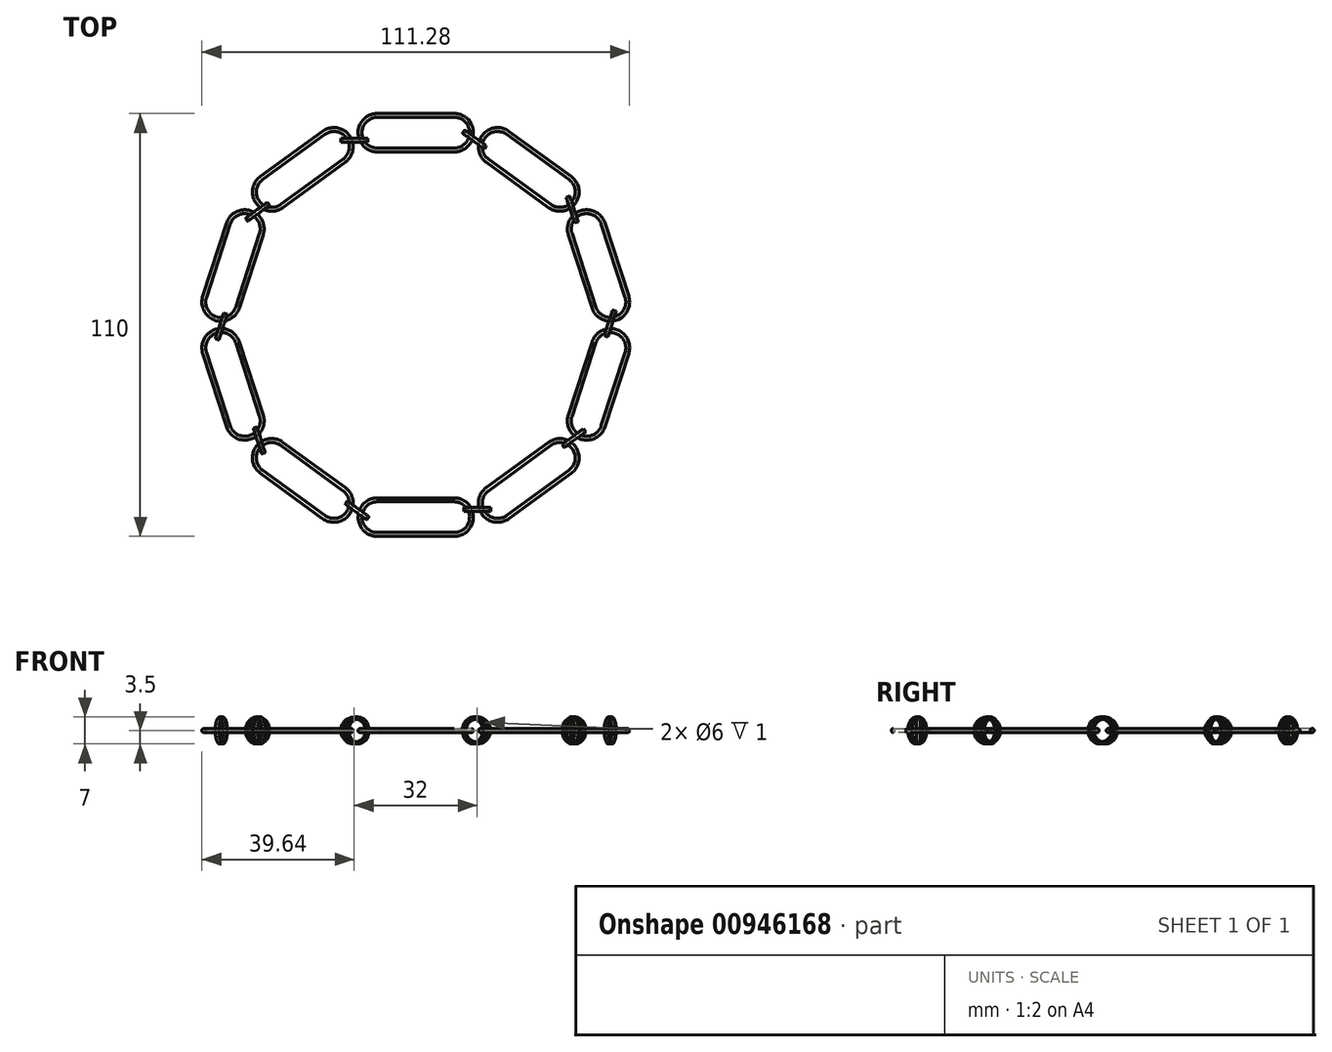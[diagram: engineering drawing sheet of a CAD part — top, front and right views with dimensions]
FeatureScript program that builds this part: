
annotation { "Feature Type Name" : "Feature", "Feature Type Description" : "" }
export const myFeature = defineFeature(function(context is Context, id is Id, definition is map)
    precondition{}
    {
        {
            var Q0;
            Q0=qCreatedBy(makeId("Top.planeOp"),FACE);
            var sketch = newSketch(context, id + "F0", { "sketchPlane" : qUnion([Q0])});
            skArc(sketch, "E0", {"start": v(-10, -45) * mm, "mid": v(-15, -50) * mm, "end": v(-10, -55) * mm});
            skArc(sketch, "E1", {"start": v(10, -55) * mm, "mid": v(15, -50) * mm, "end": v(10, -45) * mm});
            skLineSegment(sketch, "E2", {"start": v(-10, -45) * mm, "end": v(10, -45) * mm});
            skLineSegment(sketch, "E3", {"start": v(-10, -55) * mm, "end": v(10, -55) * mm});
            skLineSegment(sketch, "E4", {"start": v(-10, -50) * mm, "end": v(10, -50) * mm, "construction": true});
            skPoint(sketch, "E5", {"position": v(0, -50) * mm});
            skLineSegment(sketch, "E6.0", {"start": v(-10, -46) * mm, "end": v(10, -46) * mm});
            skArc(sketch, "E6.1", {"start": v(-10, -46) * mm, "mid": v(-14, -50) * mm, "end": v(-10, -54) * mm});
            skLineSegment(sketch, "E6.2", {"start": v(-10, -54) * mm, "end": v(10, -54) * mm});
            skArc(sketch, "E6.3", {"start": v(10, -54) * mm, "mid": v(14, -50) * mm, "end": v(10, -46) * mm});
            skSolve(sketch);
        }
        {
            var Q0;
            Q0=makeQuery(id+"F0.imprint","IMPRINT",FACE,{"disambiguationData":[TD([[makeQuery(id+"F0.imprint","IMPRINT",EDGE,{"derivedFrom":sQuery(id+"F0.wireOp",EDGE,"E0")}),1.0]])]});
            extrude(context, id + "F1", {"entities" : qUnion([Q0]), "depth" : 1 * mm, "offsetDistance" : 25 * mm});
        }
        {
            var Q0;
            Q0=makeQuery(id+"F1.opExtrude","CAP_EDGE",EDGE,{"disambiguationData":[OSD([sQuery(id+"F0.wireOp",EDGE,"E6.0")])],"isStart":false});
            var Q1;
            Q1=makeQuery(id+"F1.opExtrude","CAP_EDGE",EDGE,{"disambiguationData":[OSD([sQuery(id+"F0.wireOp",EDGE,"E6.0")])],"isStart":true});
            var Q2;
            Q2=makeQuery(id+"F1.opExtrude","CAP_EDGE",EDGE,{"disambiguationData":[OSD([sQuery(id+"F0.wireOp",EDGE,"E1")])],"isStart":false});
            var Q3;
            Q3=makeQuery(id+"F1.opExtrude","CAP_EDGE",EDGE,{"disambiguationData":[OSD([sQuery(id+"F0.wireOp",EDGE,"E1")])],"isStart":true});
            fillet(context, id + "F2", {"entities" : qUnion([Q0, Q1, Q2, Q3]), "radius" : 0.5 * mm, "tangentPropagation" : true, "allowEdgeOverflow" : false});
        }
        {
            var Q0;
            Q0=qCreatedBy(makeId("Front.planeOp"),FACE);
            cPlane(context, id + "F3", {"entities" : qUnion([Q0]), "cplaneType" : CPlaneType.OFFSET, "offset" : 48 * mm, "width" : 150 * mm, "height" : 150 * mm});
        }
        {
            var Q0;
            Q0=qCreatedBy(id+"F3.planeOp",FACE);
            var sketch = newSketch(context, id + "F4", { "sketchPlane" : qUnion([Q0])});
            skCircle(sketch, "E7", {"center": v(16, 0.5) * mm, "radius": 3.5 * mm});
            skCircle(sketch, "E8", {"center": v(16, 0.5) * mm, "radius": 3 * mm});
            skSolve(sketch);
        }
        {
            var Q0;
            Q0=makeQuery(id+"F4.imprint","IMPRINT",FACE,{"disambiguationData":[TD([[makeQuery(id+"F4.imprint","IMPRINT",EDGE,{"derivedFrom":sQuery(id+"F4.wireOp",EDGE,"E7")}),1.0]])]});
            extrude(context, id + "F5", {"entities" : qUnion([Q0]), "endBound" : BoundingType.SYMMETRIC, "depth" : 1 * mm, "offsetDistance" : 25 * mm});
        }
        {
            var Q0;
            Q0=qCreatedBy(makeId("Front.planeOp"),FACE);
            var sketch = newSketch(context, id + "F6", { "sketchPlane" : qUnion([Q0])});
            skLineSegment(sketch, "E9", {"start": v(0, 5.55) * mm, "end": v(0, -5.56) * mm, "construction": true});
            skSolve(sketch);
        }
        {
            var Q0;
            Q0=makeQuery(id+"F1.opExtrude","SWEPT_BODY",BODY,{"disambiguationData":[OSD([sQuery(id+"F0.wireOp",EDGE,"E0"),sQuery(id+"F0.wireOp",EDGE,"E1"),sQuery(id+"F0.wireOp",EDGE,"E2"),sQuery(id+"F0.wireOp",EDGE,"E3"),sQuery(id+"F0.wireOp",EDGE,"E6.0"),sQuery(id+"F0.wireOp",EDGE,"E6.1"),sQuery(id+"F0.wireOp",EDGE,"E6.2"),sQuery(id+"F0.wireOp",EDGE,"E6.3")])]});
            var Q1;
            Q1=makeQuery(id+"F5.opExtrude","SWEPT_BODY",BODY,{"disambiguationData":[OSD([sQuery(id+"F4.wireOp",EDGE,"E7"),sQuery(id+"F4.wireOp",EDGE,"E8")])]});
            var Q2;
            Q2=sQuery(id+"F6.wireOp",EDGE,"E9");
            circularPattern(context, id + "F7", {"entities" : qUnion([Q0, Q1]), "axis" : qUnion([Q2]), "angle" : 360 * degree, "instanceCount" : 10, "equalSpace" : true});
        }
    });
